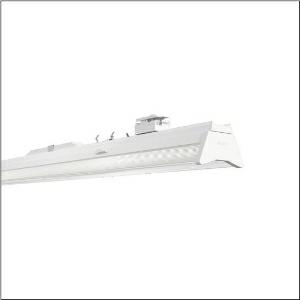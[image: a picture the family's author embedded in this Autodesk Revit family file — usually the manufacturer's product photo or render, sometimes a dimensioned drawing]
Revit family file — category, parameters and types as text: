
# Revit family: licross_r__21_performance_mo_51td16vnd45g_fcc4
name_source: partatom
category: Lighting Fixtures
units: mm (PartAtom-declared; Revit-internal decimal feet)

## family parameters
Cut with Voids When Loaded = No
Host = Face
Light Source = No
Part Type = Normal
Room Calculation Point = No
Round Connector Dimension = Use Diameter
Shared = No

## types (1)
- --- (1 x LED, 4500 lm, 26.3 W, 4000K)
    Apparent Load = 26 VA
    CIE Flux Codes = 66 88 96 79 100
    Color Rendering = 90
    Color Temperature = 4000K
    Default Elevation = 1800 mm
    Description = Licross® 21 Performance MO, luminaire insert, of sheet steel, galvanised, coil coated, white, length: 1.500mm, width: 120mm, height: 123mm, LED rated luminous flux: 4.500lm, light colour: 940, control gear: DALI 2, CLO, with plug, 5-pole, with phase selection, mains connection: 220..240V, AC, 50/60Hz, start of lifetime: 26W, end of service life: 29W, internal wiring halogen-free, primary light control with lens, of plastic, primary optical cover: cover, of PMMA, light emission: direct/indirect distribution, primary light characteristic: symmetric, protection rating (complete): IP54, insulation class (complete): insulation class I (protective earthing), certification: CE, ENEC, VDE, UKCA, protection symbol: D if used in an environment with non-conductive dust loads with corresponding accessories, impact resistance: IK06, permissible ambient temperature for indoor applications: -25..+45°C, corresponds to IFS (International Featured Standards) requirements for safety and quality in the food industry, reducing of maximum allowable ambient temperature of 5°C with ceiling mounting, LABS conformity tested according to VDMA 24364:2018-05, packaging unit: 1 piece
    Height = 114 mm
    Lamp = 1 x LED
    Lamp Light Flux = 4500 lm
    Lamp Power = 26.3 W
    Lamp count = 1
    Length = 1500 mm
    Luminous efficacy = 171 lm/W
    Manufacturer = Siteco
    ModVariant = No
    Model = 51TD16VND45G
    Mounting Place = Ceiling
    Mounting Type = Pendant
    Number of Poles = 1
    OnlyDefault = Yes
    Power Factor = 1
    Product Name = Licross® 21 Performance MO
    Product group = luminaire insert | ceiling pendant
    ProductGroupID = 902
    Protection Class = Protection class I
    Protection Degree = IP 54
    RLX_Detail_Level = 1
    RLX_Emergency_Light_Flux = 0 lm
    RLX_Emergency_Type = 0
    RLX_Emergency_Type_DB = No
    RlxData = <blob elided: 33985 chars, md5=938fc858>
    Socket = socket
    Standby Power = 0 W
    System Light Flux = 4500 lm
    System Power = 26 W
    Type Comments = factory setting: luminous flux: 100 % | dim-lin: 254 | 174 mA
    Type Image = l_1256138.jpg
    URL = http://relux.com
    VarID = @adj_069971
    Voltage = 0 V
    Weight = 0.00 kg
    Width = 120 mm

## geometry (parser evidence)
native form markers: Blend x4, Sweep x12
no freeform markers — native parametric forms only
